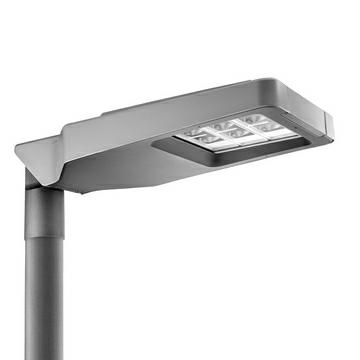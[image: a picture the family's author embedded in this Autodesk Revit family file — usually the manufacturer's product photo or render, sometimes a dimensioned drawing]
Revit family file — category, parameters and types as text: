
# Revit family: Lighting-Stradale-GEWISS-ROAD[5]MINI-LED_OTTICA_WIDE_CLI
name_source: partatom
category: Apparecchi per illuminazione
units: mm (PartAtom-declared; Revit-internal decimal feet)

## family parameters
Basato su piano di lavoro = No
Condiviso = No
Punto di calcolo locali = No
Quota connettore circolare = Usa diametro
Sempre verticale = Sì
Sorgente d'illuminazione = No
Taglio con vuoti quando caricato = No
Tipo di parte = Normale

## types (1)
- Lighting-Stradale-GEWISS-ROAD[5]MINI-LED_OTTICA_WIDE_CLI
    Alimentatore = Incluso
    Apparecchio a ridotta temperatura superficiale = -
    Applicazione = Esterno
    Cablaggio = Sezionatore
    Caratteristiche elettriche e gestione della luce = -
    Caratteristiche ottiche e illuminotecniche = -
    Carico apparente = 53 VA
    Catalogo = LIGHTING
    Catalogo Serie = ROAD [5]
    Certificazione DIN 18032-3 = -
    Certificazioni e classificazioni = -
    Classe fotobiologica = RG0
    Classe isolamento = I
    Classificazione: = -
    Codice Electrocod = 244C
    Codice digitale univoco (Datamatrix) = Attualmente non presente
    Colore = Grigio grafite
    Commenti sul wattaggio = 53W
    Contesto = Illuminazione stradale e parcheggi
    Controllo abbagliamento e luminanza = G*3 - ULOR = 0
    Corpo = Alluminio pressofuso
    Corrente di pilotaggio. = 0,7A
    Descrizione = GWR5772M30K - ROAD5 MINI WIDE 2M 3000K 0,7A CL1 1-10V
    Dispositivo di protezione = DM 10KV / CM 10KV
    Distanza minima dall'oggetto illuminato = 1M
    Durata di vita = L90B10 (Tq+25°C) = 100.000 h - L90B10 (Tq+50°C) = 75.000 h
    Efficienza luminosa (lm/W) = 102
    Finitura colore = Verniciato a polveri
    Fissaggio = Testa palo - Sbraccio
    Flusso nominale (lm) = 5400
    Frequenza nominale (Hz) = 50 / 60
    Funzionalità alimentatore = Dimmerabile
    Gancio di chiusura = Maniglia frontale integrata
    Garanzia = 5 anni
    Grado di protezione = IP66
    Gruppo ottico = Riflettore in PC metallizzato
    Guarnizioni = silicone antinvecchiamento
    IDF = f8532b79-0f86-4dcf-beb2-9edbbddadd7e
    IDT = 022a80ee4c80461ea9288278e8deede6
    IPEA = STRADALE = A++ // GRANDI AREE = A3+ // CICLOPEDONALI = A++ // AREE VERDI = A++ // CENTRO STORICO = A5+
    Immagine tipo = GWR5276M.jpg
    Inclinazione = -20° ÷ +10° sbraccio - -10° ÷ +20° testa palo
    Indice di resa cromatica = CRI-70
    Informazioni generali = -
    Installazione e manutenzione = -
    LED Life Time (L80B05) = 77000H
    Lampada: = LED
    Lumen output (lm) = 5500
    Materiali = -
    Modello = GWR5772M30K
    Norma di riferimento = EN 60598-2-3, EN 60598-1 IEC/TR 62778
    Numero moduli = 2 (2x3 LED)
    Ottica = WIDE
    Peso (kg): = 6,6
    Potenza assorbita : = 54 W @ 0.7A
    Potenza di sistema = 53W
    Produttore = GEWISS S.p.A.
    Regolazione inclinazione = -20° ÷ +10° sbraccio - -10° ÷ +20° testa palo
    Resistenza agli urti = IK08
    Resistenza al filo incandescente = -
    Resistenza alle sovratensioni : = 10 KV in modalità comune e differenziale
    SEO = Stradale
    Scheda Tecnica = https://www.gewiss.com
    Schermo = Vetro piano temperato spessore 4mm
    Sistema di controllo = Dimmerabile 1-10 V
    Sostituibilità gruppo ottico = Non disponibile
    Sostituibilità piastra di cablaggio = Non disponibile
    Superficie massima esposta al vento = 0,149999999999999M2
    Superficie massima esposta al vento : = 0,15 m²
    Temperatura di colore = 3000K
    Temperatura di colore: = 3000 K (CRI>80)
    Temperatura di esercizio = -25 +50 °C
    Temperatura di stoccaggio = -
    Temperatura di utilizzo = -25 +50 °C
    Tensione = 220/240 V - 50/60 Hz - Dimmerabile 1-10 V
    Tensione di alimentazione = 220 - 240 V
    Tipo alimentatore = Driver Led in corrente continua
    Tipo di apparecchio = Apparecchiatura stradale a LED
    Tipo di installazione e montaggio = Testa palo - Sbraccio
    Tipologia = Dimmerabile
    Tipologia sorgente luminosa = LED - Non sostituibile
    Tolleranza cromatica = SDCM = 5
    URL = https://www.gewiss.com
    Vano di alimentazione = Integrato
    Versione file RFA = 20.11
    Viti esterne = Acciaio inox
